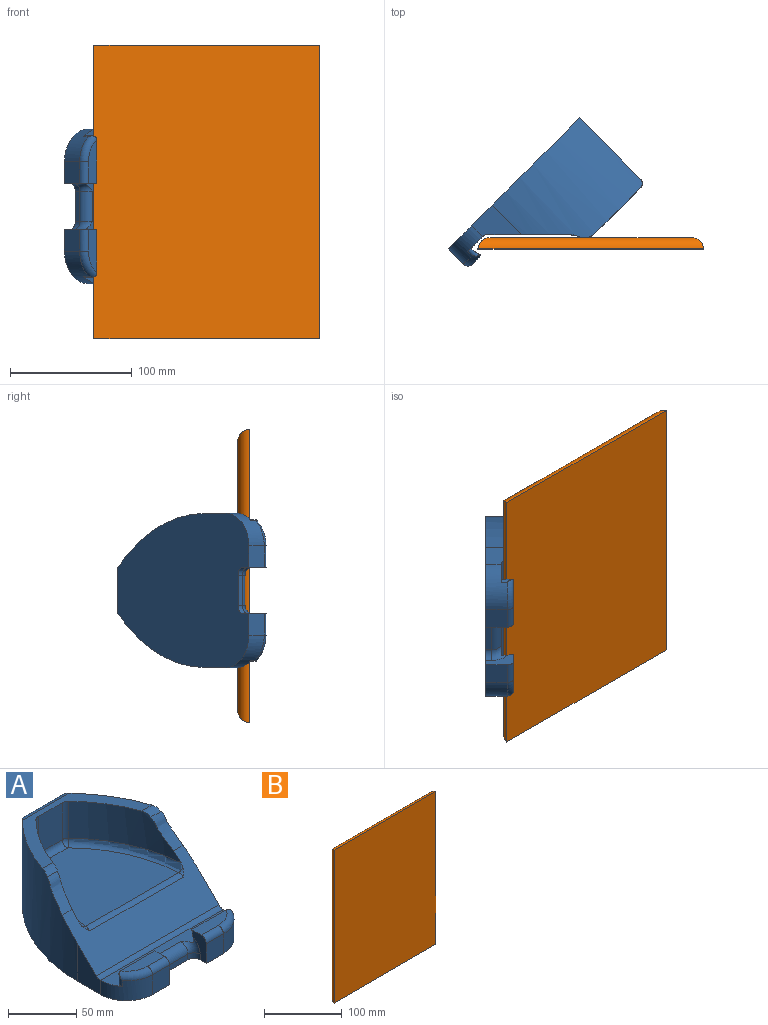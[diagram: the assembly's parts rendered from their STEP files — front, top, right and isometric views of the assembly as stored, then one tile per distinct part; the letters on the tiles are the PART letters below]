
ASSEMBLY  parts=2 mates=1
PART A: 51 faces, bbox 128.5x155.7x77.3 mm
  f0: plane 40.9x11.27mm, normal (0,0.97,-0.22), area 398.9mm2, adj f16,f18,f21,f25,f49
  f1: plane 40.9x11.27mm, normal (0,0.97,-0.22), area 398.9mm2, adj f16,f19,f22,f27,f50
  f2: torus R=21.87mm, axis (0,0,-1), area 193.8mm2, adj f19,f29,f31,f50
  f3: torus R=21.87mm, axis (0,0,-1), area 193.8mm2, adj f18,f30,f32,f49
  f4: extruded ~22.74x19.15mm, area 310.7mm2, adj f5,f11,f34,f36
  f5: cylinder r=10.16mm len=12.86mm, axis (1,0,0), area 84.9mm2, adj f4,f8,f34,f36
  f6: plane 71.12x38.1mm, normal (0,1,0), area 2709.7mm2, adj f7,f14,f33,f34
  f7: plane 152.4x127mm, normal (0,0,-1), area 15790.3mm2, adj f6,f9,f10,f15,f17,f21,f22,f23
  f8: plane 113.36x53.62mm, normal (0,0,1), area 1433.3mm2, adj f5,f13,f14,f33,f34,f36,f37,f38
  f9: plane 33.92x23.85mm, normal (1,0,0), area 528.8mm2, adj f7,f11,f20,f29,f33
  f10: plane 33.92x23.85mm, normal (-1,0,0), area 528.8mm2, adj f7,f11,f20,f30,f34
  f11: plane 127.84x36.76mm, normal (0,-0.71,0.71), area 4338mm2, adj f4,f9,f10,f12,f20,f33,f34,f36
  f12: extruded ~22.74x19.15mm, area 310.7mm2, adj f11,f13,f33,f37
  f13: cylinder r=10.16mm len=12.86mm, axis (1,0,0), area 84.9mm2, adj f8,f12,f33,f37
  f14: cylinder r=5.08mm len=48.53mm, axis (-1,0,0), area 345.6mm2, adj f6,f8,f33,f34
  f15: plane 17.78x17.65mm, normal (0,-1,0), area 313.8mm2, adj f7,f21,f30,f32
  f16: plane 127.84x17.97mm, normal (0,0,1), area 1535.1mm2, adj f0,f1,f20,f24,f25,f27,f29,f30
  f17: plane 17.78x17.65mm, normal (0,-1,0), area 313.8mm2, adj f7,f22,f29,f31
  f18: plane 35.85x9.97mm, normal (0,0,1), area 303.2mm2, adj f0,f3,f21,f32
  f19: plane 35.85x9.97mm, normal (0,0,1), area 303.2mm2, adj f1,f2,f22,f31
  f20: cylinder r=6.35mm len=127mm, axis (1,0,0), area 633.4mm2, adj f9,f10,f11,f16
  f21: plane 22.86x15.05mm, normal (1,0,0), area 209.8mm2, adj f0,f7,f15,f18,f25,f26,f32
  f22: plane 22.86x15.05mm, normal (-1,0,0), area 209.8mm2, adj f1,f7,f17,f19,f27,f28,f31
  f23: plane 25.4x5.08mm, normal (0,-1,0), area 129mm2, adj f7,f24,f26,f28
  f24: cylinder r=7.62mm len=25.4mm, axis (-1,0,0), area 304mm2, adj f16,f23,f25,f27
  f25: torus R=13.97mm, axis (-1,0,0), area 105.5mm2, adj f0,f16,f21,f24,f26
  f26: cylinder r=6.35mm len=6.35mm, axis (0,0,1), area 50.7mm2, adj f7,f21,f23,f25
  f27: torus R=13.97mm, axis (-1,0,0), area 105.5mm2, adj f1,f16,f22,f24,f28
  f28: cylinder r=6.35mm len=6.35mm, axis (0,0,-1), area 50.7mm2, adj f7,f22,f23,f27
  f29: cylinder r=26.95mm len=26.95mm, axis (0,0,1), area 655.8mm2, adj f2,f7,f9,f16,f17,f50
  f30: cylinder r=26.95mm len=26.95mm, axis (0,0,1), area 655.7mm2, adj f3,f7,f10,f15,f16,f49
  f31: cylinder r=5.08mm len=17.65mm, axis (1,0,0), area 140.7mm2, adj f2,f17,f19,f22
  f32: cylinder r=5.08mm len=17.65mm, axis (1,0,0), area 140.7mm2, adj f3,f15,f18,f21
  f33: cylinder r=138.34mm len=101.6mm, axis (0,0,1), area 7820.6mm2, adj f6,f7,f8,f9,f11,f12,f13,f14
  f34: cylinder r=138.34mm len=101.6mm, axis (0,0,1), area 7820.6mm2, adj f4,f5,f6,f7,f8,f10,f11,f14
  f35: plane 96.14x79.55mm, normal (0,0,1), area 5775.5mm2, adj f41,f43,f44,f45,f46,f47
  f36: cylinder r=128.18mm len=80.26mm, axis (0,0,1), area 2458.7mm2, adj f4,f5,f8,f11,f40,f43
  f37: cylinder r=128.18mm len=80.26mm, axis (0,0,1), area 2458.7mm2, adj f8,f11,f12,f13,f39,f47
  f38: plane 33.02x24.7mm, normal (0,-1,0), area 815.6mm2, adj f8,f39,f40,f45
  f39: cylinder r=6.35mm len=33.02mm, axis (0,0,1), area 167.2mm2, adj f8,f37,f38,f46
  f40: cylinder r=6.35mm len=33.02mm, axis (0,0,1), area 167.2mm2, adj f8,f36,f38,f44
  f41: cylinder r=6.35mm len=96.51mm, axis (-1,0,0), area 480.4mm2, adj f11,f35,f42,f48
  f42: bspline ~10.43x7.37mm, area 15.4mm2, adj f11,f41,f43
  f43: torus R=123.1mm, axis (0,0,1), area 721.2mm2, adj f11,f35,f36,f42,f44
  f44: torus R=1.27mm, axis (0,0,1), area 28.7mm2, adj f35,f40,f43,f45
  f45: cylinder r=5.08mm len=24.7mm, axis (-1,0,0), area 197.1mm2, adj f35,f38,f44,f46
  f46: torus R=1.27mm, axis (0,0,1), area 28.7mm2, adj f35,f39,f45,f47
  f47: torus R=123.1mm, axis (0,0,1), area 721.2mm2, adj f11,f35,f37,f46,f48
  f48: bspline ~10.43x7.37mm, area 15.4mm2, adj f11,f41,f47
  f49: cylinder r=3.19mm len=10.16mm, axis (0,0,1), area 27.6mm2, adj f0,f3,f16,f30
  f50: cylinder r=3.19mm len=10.16mm, axis (0,0,1), area 27.6mm2, adj f1,f2,f16,f29
PART B: 6 faces, bbox 185.7x9.4x241.3 mm
  f0: plane 241.3x185.67mm, normal (0,-1,0), area 44803.1mm2, adj f2,f3,f4,f5
  f1: plane 221.04x165.41mm, normal (0,1,0), area 36562mm2, adj f2,f3,f4,f5
  f2: cylinder r=10.16mm len=185.67mm, axis (1,0,0), area 2704.7mm2, adj f0,f1,f3,f4
  f3: cylinder r=10.16mm len=241.3mm, axis (0,0,-1), area 3550mm2, adj f0,f1,f2,f5
  f4: cylinder r=10.16mm len=241.3mm, axis (0,0,-1), area 3550mm2, adj f0,f1,f2,f5
  f5: cylinder r=10.16mm len=185.67mm, axis (1,0,0), area 2704.7mm2, adj f0,f1,f3,f4
PLACE A rot(axis=(0.36,0.86,-0.36),98.4deg) t=(-248.93,-77.87,-19.81)mm
PLACE B t=(-224.63,-78.11,-192.07)mm
MATE parallel A.f11 <-> B.f1  axis (0,-1,0) through (-198.53,-65.93,-83.31)mm
